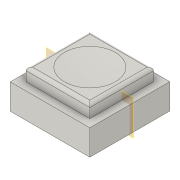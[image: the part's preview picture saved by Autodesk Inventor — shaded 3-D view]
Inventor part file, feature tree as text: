
AUTODESK INVENTOR PART (.ipt)
format: ipt  version: 2019 (Build 230136000, 136)  size: 117,248 bytes
history: native  units: mm
features: sketch x3, extrude x2, plane x1, revolve x1, fillet x1, projected_geometry x1
ambient origin geometry x8: Origin, YZ Plane, XZ Plane, XY Plane, X Axis, Y Axis, Z Axis, Center Point
bodies: Solid1 (feature_tree)
feature tree (9):
  extrude  "Extrusion1"  Depth=12.55mm
  extrude  "Extrusion2"  Depth=10.0mm
  plane  "Work Plane1"
  revolve  "Revolution1"  [1 undecoded]
  fillet  "Fillet1"  Radius=1.25mm
  sketch  "Sketch1"  dims[d0=12.5mm d1=12.55mm]
  sketch  "Sketch2"  dims[d2=4.0mm d3=0.0mm d4=10.0mm]
  sketch  "Sketch3"  dims[d5=10.0mm d6=1.25mm d7=1.25mm d8=2.0mm d9=0.0mm d10=0.5mm d11=4.0mm d12=4.0mm d13=90.0deg d14=0.5mm]
  projected_geometry  "Projected Loop1"
note: 1 required parameter value undecoded (feature->parameter linkage not recoverable at this tier; creation-order binding heuristic only, values carry confidence <= 0.55)
